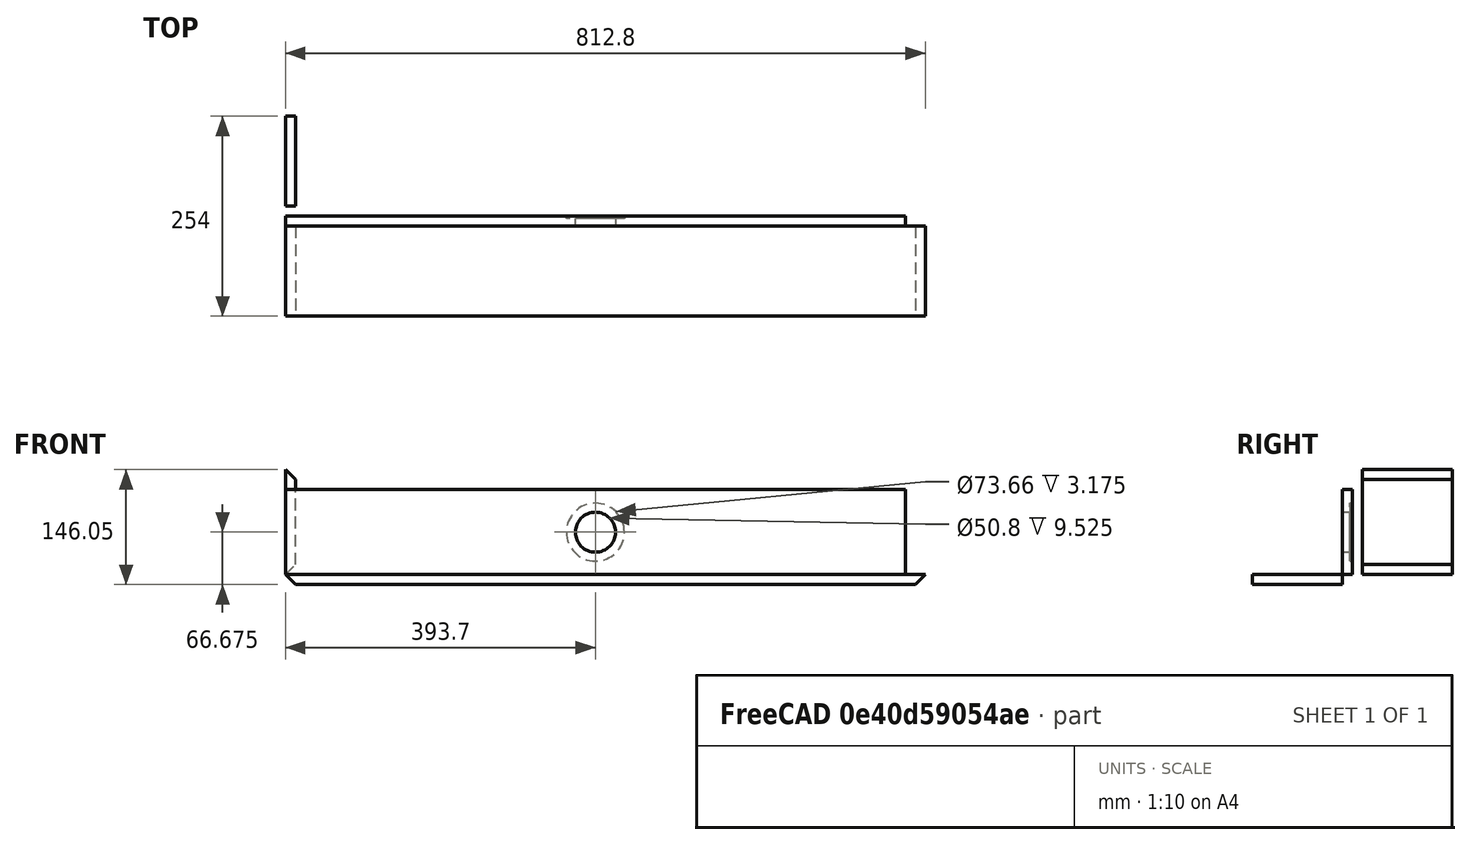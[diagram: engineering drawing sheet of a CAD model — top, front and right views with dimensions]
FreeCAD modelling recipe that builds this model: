
FCSTD DOCUMENT  (FreeCAD 0.21R33771 (Git))
Label: Overnight Sensations Center MMTMM
License: All rights reserved
LicenseURL: http://en.wikipedia.org/wiki/All_rights_reserved
objects: Sketcher::SketchObject×8, PartDesign::Body×6, App::Part×6, TechDraw::DrawViewDimension×6, PartDesign::Pad×4, PartDesign::Pocket×4, TechDraw::DrawViewPart×4, PartDesign::FeatureBase×2, Spreadsheet::Sheet×1, App::DocumentObjectGroup×1, TechDraw::DrawSVGTemplate×1, TechDraw::DrawPage×1
note: 42 computed .brp shape members not serialized (recipe doc carries the construction recipe); baked Part::Feature solids carry a one-line shape summary decoded from their .brp

FEATURE [Spreadsheet::Sheet] Spreadsheet
  cells = A1='Speaker Height; B1(height)==5.25 "; A2='Speaker Width; B2(width)==32 "; A3='Speaker Depth; B3(depth)==5 "; A4='Material Thickness; B4(thickness)==0.5 "; A6='Mid From Center; B6(mid_from_center)==3 "; A7='Low From Center; B7(low_from_center)==7.5 "; A9='Driver Dimensions; B9='diameter; A10='HiVi B3N Diameter; B10(driver_diameter)==3.5 "; C10='https://www.parts-express.com/HiVi-B3N-3-Aluminum-Driver-Round-Frame-297-428?quantity=1; A11='HiVi B4N Cutout Diameter; B11(driver_cutout_diameter)==2.875 "; A12='HiVi B4N Depth; B12(driver_depth)==2.125 "; A13='HiVi B4N Recess; B13(driver_recess)==0.125 "; A15='HiVi T20 Diameter; B15(tweeter_diameter)==2 "; C15='https://www.parts-express.com/HiVi-T20-8-3-4-20mm-Textile-Dome-Tweeter-8-Ohm-297-464?quantity=1; A16='HiVi T20 Cutout Diameter; B16(tweeter_cutout_diameter)==1.385 "; A17='HiVi T20 Depth; B17==0.5 "; A18='HiVi T20 Recess; B18(tweeter_recess)==0.1875 "; A20='Terminal Diameter; B20(terminal_diameter)==2.9 "; A21='Terminal Cutout Diameter; B21(terminal_cutout_diameter)==2 "; A22='Terminal Recess; B22(terminal_recess)==0.125 "; A23='Terminal Depth; B23(terminal_depth)==1 "
FEATURE [PartDesign::Body] Body
  Origin = -> Origin001
FEATURE [Sketcher::SketchObject] Sketch
  FullyConstrained = true
  MapMode = 5
  Placement = pos=(0,0,0) rot=(1,0,0;1.5708rad)
  Support = -> [XZ_Plane004]
  expr: Constraints[10] = Spreadsheet.height
  expr: Constraints[9] = Spreadsheet.width
  sketch-geometry (4):
    g0: LineSegment StartX=0 StartY=0 StartZ=0 EndX=812.8 EndY=0 EndZ=0
    g1: LineSegment StartX=812.8 StartY=0 StartZ=0 EndX=812.8 EndY=133.35 EndZ=0
    g2: LineSegment StartX=812.8 StartY=133.35 StartZ=0 EndX=0 EndY=133.35 EndZ=0
    g3: LineSegment StartX=0 StartY=133.35 StartZ=0 EndX=0 EndY=0 EndZ=0
  constraints (11):
    c: Coincident(g0,g1)
    c: Coincident(g1,g2)
    c: Coincident(g2,g3)
    c: Coincident(g3,g0)
    c: Horizontal(g0)
    c: Horizontal(g2)
    c: Vertical(g1)
    c: Vertical(g3)
    c: Coincident(g0,g-1)
    c: DistanceX(g0,g0) = 812.8
    c: DistanceY(g3,g3) = 133.35
FEATURE [PartDesign::Pad] Pad
  Direction = (0,-1,-2e-16)
  Length = 12.7
  Length2 = 10
  Placement = pos=(0,0,0) rot=(1,0,0;1.5708rad)
  Profile = -> Sketch
  ReferenceAxis = -> Sketch [N_Axis]
  Type = 0
FEATURE [Sketcher::SketchObject] Sketch001
  ExternalGeometry = -> [Pad]
  FullyConstrained = true
  MapMode = 5
  Placement = pos=(0,-12.7,0) rot=(1,0,0;1.5708rad)
  Support = -> [Pad]
  expr: Constraints[10] = Spreadsheet.mid_from_center
  expr: Constraints[11] = Spreadsheet.low_from_center
  expr: Constraints[1] = Spreadsheet.tweeter_cutout_diameter
  expr: Constraints[2] = Spreadsheet.driver_cutout_diameter
  expr: Constraints[6] = Spreadsheet.mid_from_center
  expr: Constraints[7] = Spreadsheet.low_from_center
  sketch-geometry (5):
    g0: Circle CenterX=406.4 CenterY=66.675 CenterZ=0 NormalX=0 NormalY=0 NormalZ=1 AngleXU=0 Radius=17.5895
    g1: Circle CenterX=330.2 CenterY=66.675 CenterZ=0 NormalX=0 NormalY=0 NormalZ=1 AngleXU=0 Radius=36.5125
    g2: Circle CenterX=215.9 CenterY=66.675 CenterZ=0 NormalX=0 NormalY=0 NormalZ=1 AngleXU=0 Radius=36.5125
    g3: Circle CenterX=596.9 CenterY=66.675 CenterZ=0 NormalX=0 NormalY=0 NormalZ=1 AngleXU=0 Radius=36.5125
    g4: Circle CenterX=482.6 CenterY=66.675 CenterZ=0 NormalX=0 NormalY=0 NormalZ=1 AngleXU=0 Radius=36.5125
  constraints (14):
    c: Symmetric(g-5,g-4,g0)
    c: Diameter(g0) = 35.179
    c: Diameter(g1) = 73.025
    c: Equal(g2,g1)
    c: Horizontal(g2,g1)
    c: Horizontal(g1,g0)
    c: DistanceX(g1,g0) = 76.2
    c: DistanceX(g2,g0) = 190.5
    c: Diameter(g4) = 73.025
    c: Equal(g3,g4)
    c: DistanceX(g0,g4) = 76.2
    c: DistanceX(g0,g3) = 190.5
    c: Horizontal(g3,g4)
    c: Horizontal(g4,g0)
FEATURE [PartDesign::Pocket] Pocket
  Direction = (0,1,2e-16)
  Length = 5
  Length2 = 5
  Placement = pos=(0,0,0) rot=(1,0,0;1.5708rad)
  Profile = -> Sketch001
  ReferenceAxis = -> Sketch001 [N_Axis]
  Type = 1
FEATURE [Sketcher::SketchObject] Sketch002
  ExternalGeometry = -> [Pocket]
  FullyConstrained = true
  MapMode = 5
  Placement = pos=(0,-12.7,0) rot=(1,0,0;1.5708rad)
  Support = -> [Pocket]
  expr: Constraints[0] = Spreadsheet.driver_diameter
  sketch-geometry (4):
    g0: Circle CenterX=215.9 CenterY=66.675 CenterZ=0 NormalX=0 NormalY=0 NormalZ=1 AngleXU=0 Radius=44.45
    g1: Circle CenterX=330.2 CenterY=66.675 CenterZ=0 NormalX=0 NormalY=0 NormalZ=1 AngleXU=0 Radius=44.45
    g2: Circle CenterX=482.6 CenterY=66.675 CenterZ=0 NormalX=0 NormalY=0 NormalZ=1 AngleXU=0 Radius=44.45
    g3: Circle CenterX=596.9 CenterY=66.675 CenterZ=0 NormalX=0 NormalY=0 NormalZ=1 AngleXU=0 Radius=44.45
  constraints (8):
    c: Diameter(g0) = 88.9
    c: Equal(g2,g3)
    c: Equal(g3,g1)
    c: Equal(g1,g0)
    c: Coincident(g1,g-4)
    c: Coincident(g0,g-3)
    c: Coincident(g2,g-6)
    c: Coincident(g3,g-7)
FEATURE [PartDesign::Pocket] Pocket001
  Direction = (0,1,2e-16)
  Length = 3.175
  Length2 = 5
  Placement = pos=(0,0,0) rot=(1,0,0;1.5708rad)
  Profile = -> Sketch002
  ReferenceAxis = -> Sketch002 [N_Axis]
  Type = 0
  expr: Length = Spreadsheet.driver_recess
FEATURE [Sketcher::SketchObject] Sketch003
  ExternalGeometry = -> [Pocket001]
  FullyConstrained = true
  MapMode = 5
  Placement = pos=(0,-12.7,0) rot=(1,0,0;1.5708rad)
  Support = -> [Pocket001]
  expr: Constraints[0] = Spreadsheet.tweeter_diameter
  sketch-geometry (1):
    g0: Circle CenterX=406.4 CenterY=66.675 CenterZ=0 NormalX=0 NormalY=0 NormalZ=1 AngleXU=0 Radius=25.4
  constraints (2):
    c: Diameter(g0) = 50.8
    c: Coincident(g0,g-4)
FEATURE [PartDesign::Pocket] Pocket002
  Direction = (0,1,2e-16)
  Length = 4.7625
  Length2 = 5
  Placement = pos=(0,0,0) rot=(1,0,0;1.5708rad)
  Profile = -> Sketch003
  ReferenceAxis = -> Sketch003 [N_Axis]
  Type = 0
  expr: Length = Spreadsheet.tweeter_recess
FEATURE [App::Part] Part  label="baffle"
  Group = -> [Body,Sketch,Pad,Sketch001,Pocket,Sketch002,Pocket001,Sketch003,Pocket002]
  Origin = -> Origin
FEATURE [Sketcher::SketchObject] Sketch004
  FullyConstrained = true
  MapMode = 5
  Placement = pos=(0,0,0) rot=(1,0,0;1.5708rad)
  Support = -> [XZ_Plane006]
  expr: Constraints[11] = Spreadsheet.thickness
  expr: Constraints[8] = Spreadsheet.width
  sketch-geometry (4):
    g0: LineSegment StartX=0 StartY=0 StartZ=0 EndX=812.8 EndY=0 EndZ=0
    g1: LineSegment StartX=800.1 StartY=12.7 StartZ=0 EndX=12.7 EndY=12.7 EndZ=0
    g2: LineSegment StartX=0 StartY=0 StartZ=0 EndX=12.7 EndY=12.7 EndZ=0
    g3: LineSegment StartX=812.8 StartY=0 StartZ=0 EndX=800.1 EndY=12.7 EndZ=0
  constraints (12):
    c: Horizontal(g0)
    c: Horizontal(g1)
    c: Coincident(g2,g0)
    c: Angle(g0,g2) = 0.785398
    c: Coincident(g3,g0)
    c: Angle(g3,g0) = 0.785398
    c: Coincident(g1,g3)
    c: Coincident(g1,g2)
    c: DistanceX(g0,g0) = 812.8
    c: PointOnObject(g0,g-1)
    c: PointOnObject(g0,g-2)
    c: Distance(g1,g0) = 12.7
FEATURE [PartDesign::Pad] Pad001
  Direction = (0,-1,-2e-16)
  Length = 114.3
  Length2 = 10
  Placement = pos=(0,0,0) rot=(1,0,0;1.5708rad)
  Profile = -> Sketch004
  ReferenceAxis = -> Sketch004 [N_Axis]
  Reversed = true
  Type = 0
  expr: Length = Spreadsheet.depth - Spreadsheet.thickness
FEATURE [PartDesign::Body] Body001
  Group = -> [Sketch004,Pad001]
  Origin = -> Origin003
  Tip = -> Pad001
FEATURE [App::Part] Part001  label="bottom"
  Group = -> [Body001]
  Origin = -> Origin002
FEATURE [PartDesign::FeatureBase] Clone
  BaseFeature = -> Body001
FEATURE [PartDesign::Body] Body002
  Group = -> [Clone]
  Origin = -> Origin004
  Placement = pos=(0,-12.7,0) rot=(1,0,0;3.14159rad)
  Tip = -> Clone
  expr: .Placement.Base.y = -Spreadsheet.thickness
FEATURE [App::Part] Part002  label="top"
  Group = -> [Body002]
  Origin = -> Origin005
  Placement = pos=(0,127,133.35) rot=(0,0,1;0rad)
  expr: .Placement.Base.y = Spreadsheet.depth
  expr: .Placement.Base.z = Spreadsheet.height
FEATURE [Sketcher::SketchObject] Sketch005
  FullyConstrained = true
  MapMode = 5
  Placement = pos=(0,0,0) rot=(1,0,0;1.5708rad)
  Support = -> [XZ_Plane010]
  expr: Constraints[11] = Spreadsheet.thickness
  expr: Constraints[4] = Spreadsheet.height
  sketch-geometry (4):
    g0: LineSegment StartX=12.7 StartY=12.7 StartZ=0 EndX=12.7 EndY=120.65 EndZ=0
    g1: LineSegment StartX=0 StartY=133.35 StartZ=0 EndX=0 EndY=0 EndZ=0
    g2: LineSegment StartX=0 StartY=0 StartZ=0 EndX=12.7 EndY=12.7 EndZ=0
    g3: LineSegment StartX=0 StartY=133.35 StartZ=0 EndX=12.7 EndY=120.65 EndZ=0
  constraints (12):
    c: Vertical(g0)
    c: Vertical(g1)
    c: PointOnObject(g1,g-2)
    c: PointOnObject(g1,g-1)
    c: DistanceY(g1,g1) = 133.35
    c: Angle(g1,g3) = 0.785398
    c: Angle(g2,g1) = 0.785398
    c: Coincident(g0,g2)
    c: Coincident(g0,g3)
    c: Coincident(g3,g1)
    c: Coincident(g2,g1)
    c: Distance(g0,g1) = 12.7
FEATURE [PartDesign::Pad] Pad002
  Direction = (0,-1,-2e-16)
  Length = 114.3
  Length2 = 10
  Placement = pos=(0,0,0) rot=(1,0,0;1.5708rad)
  Profile = -> Sketch005
  ReferenceAxis = -> Sketch005 [N_Axis]
  Reversed = true
  Type = 0
  expr: Length = Spreadsheet.depth - Spreadsheet.thickness
FEATURE [PartDesign::Body] Body003
  Group = -> [Sketch005,Pad002]
  Origin = -> Origin007
  Tip = -> Pad002
FEATURE [App::Part] Part003  label="left"
  Group = -> [Body003]
  Origin = -> Origin006
FEATURE [PartDesign::FeatureBase] Clone001
  BaseFeature = -> Body003
  Placement = pos=(0,12.7,0) rot=(0,0,1;0rad)
  expr: .Placement.Base.y = Spreadsheet.thickness
FEATURE [PartDesign::Body] Body004
  Group = -> [Clone001]
  Origin = -> Origin009
  Tip = -> Clone001
FEATURE [App::Part] Part004  label="right"
  Group = -> [Body004]
  Origin = -> Origin008
  Placement = pos=(812.8,127,0) rot=(0,0,1;3.14159rad)
  expr: .Placement.Base.x = Spreadsheet.width
  expr: .Placement.Base.y = Spreadsheet.depth
FEATURE [Sketcher::SketchObject] Sketch006
  FullyConstrained = true
  MapMode = 5
  Placement = pos=(0,0,0) rot=(1,0,0;1.5708rad)
  Support = -> [XZ_Plane014]
  expr: Constraints[10] = Spreadsheet.width - 2 * Spreadsheet.thickness
  expr: Constraints[11] = Spreadsheet.height - 2 * Spreadsheet.thickness
  expr: Constraints[13] = Spreadsheet.terminal_cutout_diameter
  sketch-geometry (5):
    g0: LineSegment StartX=0 StartY=0 StartZ=0 EndX=787.4 EndY=0 EndZ=0
    g1: LineSegment StartX=787.4 StartY=0 StartZ=0 EndX=787.4 EndY=107.95 EndZ=0
    g2: LineSegment StartX=787.4 StartY=107.95 StartZ=0 EndX=0 EndY=107.95 EndZ=0
    g3: LineSegment StartX=0 StartY=107.95 StartZ=0 EndX=0 EndY=0 EndZ=0
    g4: Circle CenterX=393.7 CenterY=53.975 CenterZ=0 NormalX=0 NormalY=0 NormalZ=1 AngleXU=0 Radius=25.4
  constraints (14):
    c: Coincident(g0,g1)
    c: Coincident(g1,g2)
    c: Coincident(g2,g3)
    c: Coincident(g3,g0)
    c: Horizontal(g0)
    c: Horizontal(g2)
    c: Vertical(g1)
    c: Vertical(g3)
    c: PointOnObject(g0,g-1)
    c: PointOnObject(g0,g-2)
    c: DistanceX(g2,g2) = 787.4
    c: DistanceY(g3,g3) = 107.95
    c: Symmetric(g2,g0,g4)
    c: Diameter(g4) = 50.8
FEATURE [PartDesign::Pad] Pad003
  Direction = (0,-1,-2e-16)
  Length = 12.7
  Length2 = 10
  Placement = pos=(0,0,0) rot=(1,0,0;1.5708rad)
  Profile = -> Sketch006
  ReferenceAxis = -> Sketch006 [N_Axis]
  Type = 0
  expr: Length = Spreadsheet.thickness
FEATURE [Sketcher::SketchObject] Sketch007
  ExternalGeometry = -> [Pad003]
  FullyConstrained = true
  MapMode = 5
  Placement = pos=(0,-1e-16,0) rot=(-1,0,0;1.5708rad)
  Support = -> [Pad003]
  expr: Constraints[1] = Spreadsheet.terminal_diameter
  sketch-geometry (1):
    g0: Circle CenterX=393.7 CenterY=-53.975 CenterZ=0 NormalX=0 NormalY=0 NormalZ=1 AngleXU=0 Radius=36.83
  constraints (2):
    c: Coincident(g0,g-3)
    c: Diameter(g0) = 73.66
FEATURE [PartDesign::Pocket] Pocket003
  BaseFeature = -> Pad003
  Direction = (0,-1,-2e-16)
  Length = 3.175
  Length2 = 5
  Placement = pos=(0,0,0) rot=(1,0,0;1.5708rad)
  Profile = -> Sketch007
  ReferenceAxis = -> Sketch007 [N_Axis]
  Type = 0
  expr: Length = Spreadsheet.terminal_recess
FEATURE [PartDesign::Body] Body005
  Group = -> [Sketch006,Pad003,Sketch007,Pocket003]
  Origin = -> Origin011
  Tip = -> Pocket003
FEATURE [App::Part] Part005  label="back"
  Group = -> [Body005]
  Origin = -> Origin010
  Placement = pos=(12.7,114.3,12.7) rot=(0,0,1;0rad)
  expr: .Placement.Base.x = Spreadsheet.thickness
  expr: .Placement.Base.y = Spreadsheet.depth - Spreadsheet.thickness
  expr: .Placement.Base.z = Spreadsheet.thickness
FEATURE [App::DocumentObjectGroup] Group  label="Speaker"
  Group = -> [Part,Part001,Part002,Part003,Part004,Part005]
FEATURE [TechDraw::DrawSVGTemplate] Template
  EditableTexts = Code=v1.0.0; CompanyAddress=https://<owner>.com; CompanyName=Stephen Houser; DrawingNumber=2024-08-06; DrawingTitle1=Overnight Sensations; DrawingTitle2=Center Speaker MMTMM; Revision=Rev; Scale=1:8; Sheet=Sheet n of m; Weight=Weight
  Height = 215.9
  Orientation = 1
  Template = <userpath>/Documents/USLetter_Landscape.svg
  Width = 279.4
FEATURE [TechDraw::DrawViewPart] View001  label="front_view"
  CoarseView = false
  Direction = (0,-1,0)
  Focus = 100
  HardHidden = false
  IsoCount = 0
  IsoHidden = false
  IsoVisible = false
  LockPosition = false
  Perspective = false
  Rotation = 0
  Scale = 0.125
  ScaleType = 2
  ScrubCount = 0
  SeamHidden = false
  SeamVisible = false
  SmoothHidden = false
  SmoothVisible = true
  Source = -> [Group]
  X = 88.9
  XDirection = (1,0,0)
  Y = 166.064
FEATURE [TechDraw::DrawViewPart] View003  label="top_view"
  CoarseView = false
  Direction = (0,0,1)
  Focus = 100
  HardHidden = false
  IsoCount = 0
  IsoHidden = false
  IsoVisible = false
  LockPosition = false
  Perspective = false
  Rotation = 0
  Scale = 0.125
  ScaleType = 2
  ScrubCount = 0
  SeamHidden = false
  SeamVisible = false
  SmoothHidden = false
  SmoothVisible = true
  Source = -> [Group]
  X = 88.9
  XDirection = (1,0,0)
  Y = 116.252
FEATURE [TechDraw::DrawViewPart] View004  label="back_view"
  CoarseView = false
  Direction = (0,1,0)
  Focus = 100
  HardHidden = false
  IsoCount = 0
  IsoHidden = false
  IsoVisible = false
  LockPosition = false
  Perspective = false
  Rotation = 0
  Scale = 0.125
  ScaleType = 2
  ScrubCount = 0
  SeamHidden = false
  SeamVisible = false
  SmoothHidden = false
  SmoothVisible = true
  Source = -> [Group]
  X = 88.9
  XDirection = (-1,0,0)
  Y = 65.8864
FEATURE [TechDraw::DrawViewDimension] Dimension
  AngleOverride = false
  Arbitrary = false
  ArbitraryTolerances = false
  EqualTolerance = true
  ExtensionAngle = 0
  FormatSpec = %.2w
  FormatSpecOverTolerance = %+.2w
  FormatSpecUnderTolerance = %+.2w
  Inverted = false
  LineAngle = 0
  LockPosition = false
  MeasureType = 1
  OverTolerance = 0
  References2D = -> [View001]
  Rotation = 0
  ScaleType = 0
  TheoreticalExact = false
  Type = 1
  UnderTolerance = 0
  X = 0.285491
  Y = -12.5434
FEATURE [TechDraw::DrawViewDimension] Dimension001
  AngleOverride = false
  Arbitrary = false
  ArbitraryTolerances = false
  EqualTolerance = true
  ExtensionAngle = 0
  FormatSpec = %.2w
  FormatSpecOverTolerance = %+.2w
  FormatSpecUnderTolerance = %+.2w
  Inverted = false
  LineAngle = 0
  LockPosition = false
  MeasureType = 1
  OverTolerance = 0
  References2D = -> [View001]
  Rotation = 0
  ScaleType = 0
  TheoreticalExact = false
  Type = 1
  UnderTolerance = 0
  X = 4.33426
  Y = 19.974
FEATURE [TechDraw::DrawViewDimension] Dimension002
  AngleOverride = false
  Arbitrary = false
  ArbitraryTolerances = false
  EqualTolerance = true
  ExtensionAngle = 0
  FormatSpec = %.2w
  FormatSpecOverTolerance = %+.2w
  FormatSpecUnderTolerance = %+.2w
  Inverted = false
  LineAngle = 0
  LockPosition = false
  MeasureType = 1
  OverTolerance = 0
  References2D = -> [View001]
  Rotation = 0
  ScaleType = 0
  TheoreticalExact = false
  Type = 1
  UnderTolerance = 0
  X = 12.1917
  Y = 30.2517
FEATURE [TechDraw::DrawViewDimension] Dimension003
  AngleOverride = false
  Arbitrary = false
  ArbitraryTolerances = false
  EqualTolerance = true
  ExtensionAngle = 0
  FormatSpec = %.2w
  FormatSpecOverTolerance = %+.2w
  FormatSpecUnderTolerance = %+.2w
  Inverted = false
  LineAngle = 0
  LockPosition = false
  MeasureType = 1
  OverTolerance = 0
  References2D = -> [View001]
  Rotation = 0
  ScaleType = 0
  TheoreticalExact = false
  Type = 2
  UnderTolerance = 0
  X = 58.651
  Y = 1.88187
FEATURE [TechDraw::DrawViewDimension] Dimension004
  AngleOverride = false
  Arbitrary = false
  ArbitraryTolerances = false
  EqualTolerance = true
  ExtensionAngle = 0
  FormatSpec = %.2w
  FormatSpecOverTolerance = %+.2w
  FormatSpecUnderTolerance = %+.2w
  Inverted = false
  LineAngle = 0
  LockPosition = false
  MeasureType = 1
  OverTolerance = 0
  References2D = -> [View003]
  Rotation = 0
  ScaleType = 0
  TheoreticalExact = false
  Type = 2
  UnderTolerance = 0
  X = 57.5439
  Y = 1.50078
FEATURE [TechDraw::DrawViewDimension] Dimension005
  AngleOverride = false
  Arbitrary = false
  ArbitraryTolerances = false
  EqualTolerance = true
  ExtensionAngle = 0
  FormatSpec = %.2w
  FormatSpecOverTolerance = %+.2w
  FormatSpecUnderTolerance = %+.2w
  Inverted = false
  LineAngle = 0
  LockPosition = false
  MeasureType = 1
  OverTolerance = 0
  References2D = -> [View004]
  Rotation = 0
  ScaleType = 0
  TheoreticalExact = false
  Type = 1
  UnderTolerance = 0
  X = 25.5784
  Y = 25.4341
FEATURE [TechDraw::DrawViewPart] View  label="iso_view"
  CoarseView = false
  Direction = (0.57735,-0.57735,0.57735)
  Focus = 100
  HardHidden = false
  IsoCount = 0
  IsoHidden = false
  IsoVisible = false
  LockPosition = false
  Perspective = false
  Rotation = 0
  Scale = 0.15
  ScaleType = 2
  ScrubCount = 0
  SeamHidden = false
  SeamVisible = false
  SmoothHidden = false
  SmoothVisible = true
  Source = -> [Group]
  X = 207.679
  XDirection = (0.707107,0.707107,0)
  Y = 127.441
FEATURE [TechDraw::DrawPage] Page
  KeepUpdated = true
  NextBalloonIndex = 1
  ProjectionType = 0
  Template = -> Template
  Views = -> [View001,View003,View004,Dimension,Dimension001,Dimension002,Dimension003,Dimension004,Dimension005,View]
